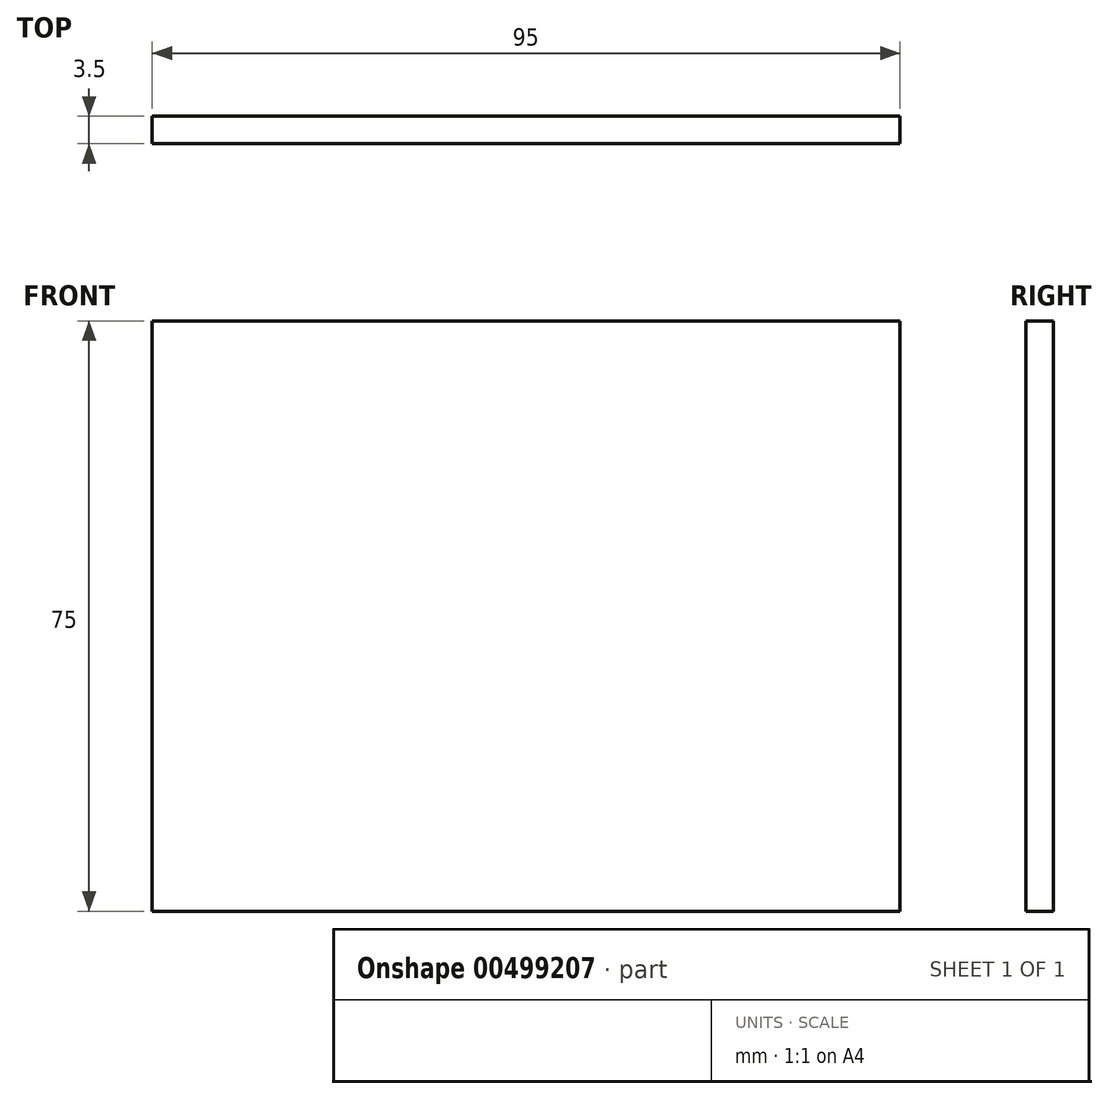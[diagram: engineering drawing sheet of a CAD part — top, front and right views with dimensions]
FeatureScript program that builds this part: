
annotation { "Feature Type Name" : "Feature", "Feature Type Description" : "" }
export const myFeature = defineFeature(function(context is Context, id is Id, definition is map)
    precondition{}
    {
        {
            var Q0;
            Q0=qCreatedBy(makeId("Front.planeOp"),FACE);
            var sketch = newSketch(context, id + "F0", { "sketchPlane" : qUnion([Q0])});
            skLineSegment(sketch, "E0.bottom", {"start": v(-47.5, 37.5) * mm, "end": v(47.5, 37.5) * mm});
            skLineSegment(sketch, "E0.top", {"start": v(-47.5, -37.5) * mm, "end": v(47.5, -37.5) * mm});
            skLineSegment(sketch, "E0.left", {"start": v(-47.5, 37.5) * mm, "end": v(-47.5, -37.5) * mm});
            skLineSegment(sketch, "E0.right", {"start": v(47.5, 37.5) * mm, "end": v(47.5, -37.5) * mm});
            skLineSegment(sketch, "E1", {"start": v(47.5, 37.5) * mm, "end": v(-47.5, -37.5) * mm, "construction": true});
            skSolve(sketch);
        }
        {
            var Q0;
            Q0 = qSketchRegion(id + "F0", true);
            extrude(context, id + "F1", {"entities" : qUnion([Q0]), "depth" : 3.5 * mm});
        }
    });
